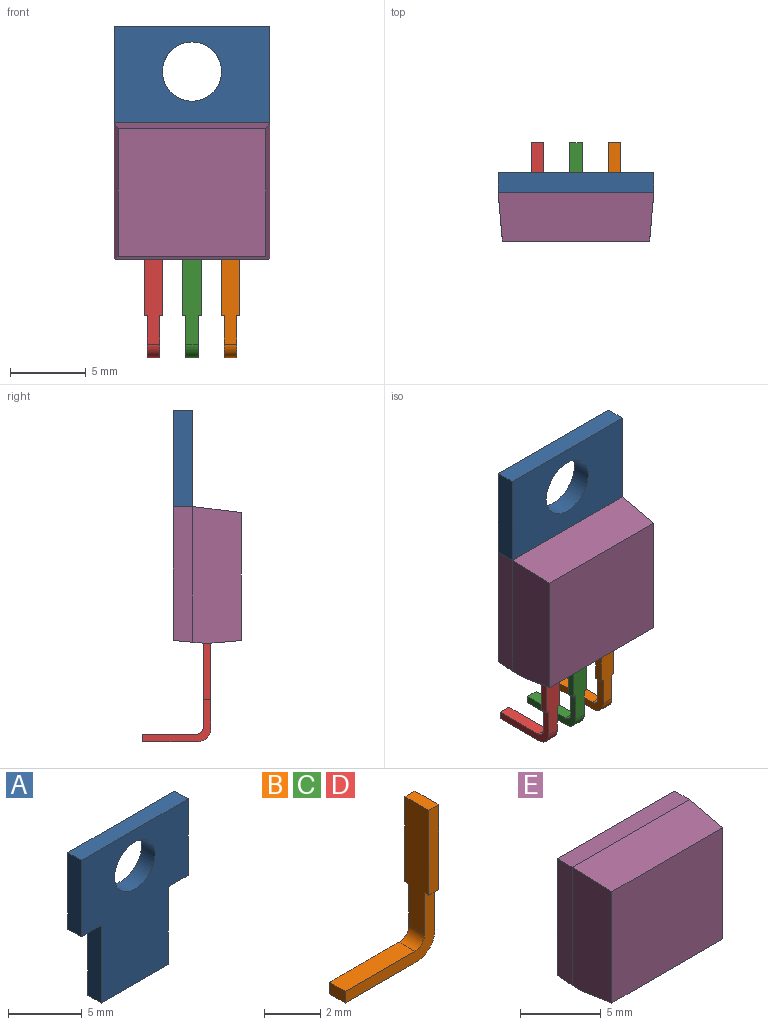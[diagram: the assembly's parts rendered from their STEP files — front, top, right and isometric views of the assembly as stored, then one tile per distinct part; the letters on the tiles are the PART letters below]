
ASSEMBLY  parts=5 mates=4
PART A: 11 faces, bbox 10.3x1.3x12.8 mm
  f0: plane 10.26x1.3mm, normal (0,0,1), area 13.3mm2, adj f1,f7,f8,f9
  f1: plane 6.35x1.3mm, normal (-1,0,0), area 8.3mm2, adj f0,f2,f8,f9
  f2: plane 1.91x1.3mm, normal (0,0,-1), area 2.5mm2, adj f1,f3,f8,f9
  f3: plane 6.45x1.3mm, normal (-1,0,0), area 8.4mm2, adj f2,f4,f8,f9
  f4: plane 6.44x1.3mm, normal (0,0,-1), area 8.4mm2, adj f3,f5,f8,f9
  f5: plane 6.45x1.3mm, normal (1,0,0), area 8.4mm2, adj f4,f6,f8,f9
  f6: plane 1.91x1.3mm, normal (0,0,-1), area 2.5mm2, adj f5,f7,f8,f9
  f7: plane 6.35x1.3mm, normal (1,0,0), area 8.3mm2, adj f0,f6,f8,f9
  f8: plane 12.8x10.26mm, normal (0,-1,0), area 94.8mm2, adj f0,f1,f2,f3,f4,f5,f6,f7
  f9: plane 12.8x10.26mm, normal (0,1,0), area 94.8mm2, adj f0,f1,f2,f3,f4,f5,f6,f7
  f10: cylinder r=1.95mm len=3.9mm, axis (0,1,0), area 15.9mm2, adj f8,f9
PART B: 14 faces, bbox 4.5x1.2x6.5 mm
  f0: plane 5.6x1.2mm, normal (1,0,0), area 6mm2, adj f6,f7,f8,f9,f10,f11,f12,f13
  f1: plane 5.5x1.2mm, normal (-1,0,0), area 5.9mm2, adj f2,f7,f8,f9,f10,f11,f12,f13
  f2: cylinder r=0.5mm len=0.8mm, axis (0,1,0), area 0.6mm2, adj f1,f3,f7,f8
  f3: plane 3.5x0.8mm, normal (0,0,1), area 2.8mm2, adj f2,f4,f7,f8
  f4: plane 0.8x0.5mm, normal (-1,0,0), area 0.4mm2, adj f3,f5,f7,f8
  f5: plane 3.6x0.8mm, normal (0,0,-1), area 2.9mm2, adj f4,f6,f7,f8
  f6: cylinder r=0.9mm len=0.9mm, axis (0,1,0), area 1.1mm2, adj f0,f5,f7,f8
  f7: plane 4.5x2.8mm, normal (0,-1,0), area 3.3mm2, adj f0,f1,f2,f3,f4,f5,f6,f9
  f8: plane 4.5x2.8mm, normal (0,1,0), area 3.3mm2, adj f0,f1,f2,f3,f4,f5,f6,f10
  f9: plane 0.5x0.2mm, normal (0,0,-1), area 0.1mm2, adj f0,f1,f7,f12
  f10: plane 0.5x0.2mm, normal (0,0,-1), area 0.1mm2, adj f0,f1,f8,f13
  f11: plane 1.2x0.5mm, normal (0,0,1), area 0.6mm2, adj f0,f1,f12,f13
  f12: plane 3.7x0.5mm, normal (0,-1,0), area 1.9mm2, adj f0,f1,f9,f11
  f13: plane 3.7x0.5mm, normal (0,1,0), area 1.9mm2, adj f0,f1,f10,f11
PART C: same geometry as B
PART D: same geometry as B
PART E: 11 faces, bbox 10.3x4.5x9 mm
  f0: plane 8.94x1.3mm, normal (1,0,0), area 11.5mm2, adj f1,f5,f7,f9
  f1: plane 10.26x1.3mm, normal (0,0,1), area 13.3mm2, adj f0,f2,f5,f6
  f2: plane 8.94x1.3mm, normal (-1,0,0), area 11.5mm2, adj f1,f5,f8,f9
  f3: plane 10.14x0.5mm, normal (0,0,-1), area 5mm2, adj f7,f8,f9,f10
  f4: plane 9.7x8.43mm, normal (0,-1,0), area 81.8mm2, adj f6,f7,f8,f10
  f5: plane 10.26x8.83mm, normal (0,1,0), area 90.5mm2, adj f0,f1,f2,f9
  f6: plane 10.26x3.2mm, normal (0,-0.12,0.99), area 32.2mm2, adj f1,f4,f7,f8
  f7: plane 9x3.2mm, normal (1,-0.09,0), area 28.1mm2, adj f0,f3,f4,f6,f9,f10
  f8: plane 9x3.2mm, normal (-1,-0.09,0), area 28.1mm2, adj f2,f3,f4,f6,f9,f10
  f9: plane 10.26x2mm, normal (0,0.09,-1), area 20.6mm2, adj f0,f2,f3,f5,f7,f8
  f10: plane 10.05x2mm, normal (0,-0.09,-1), area 19.8mm2, adj f3,f4,f7,f8
PLACE A t=(30.13,0,-18.01)mm
PLACE B rot(axis=(0,0,-1),90deg) t=(2.54,-49.26,1.64)mm
PLACE C rot(axis=(0,0,-1),90deg) t=(0,-49.26,1.64)mm
PLACE D rot(axis=(0,0,-1),90deg) t=(-2.54,-49.26,1.64)mm
PLACE E t=(30.13,0,-3.36)mm
MATE fastened E.f3 <-> D.f11  axis (0,0,-1) through (0,-2,-12.36)mm
MATE fastened A.f2 <-> E.f1  axis (0,0,1) through (0,0,-3.36)mm
MATE fastened E.f3 <-> C.f11  axis (0,0,-1) through (0,-2,-12.36)mm
MATE fastened E.f3 <-> B.f11  axis (0,0,-1) through (0,-2,-12.36)mm
